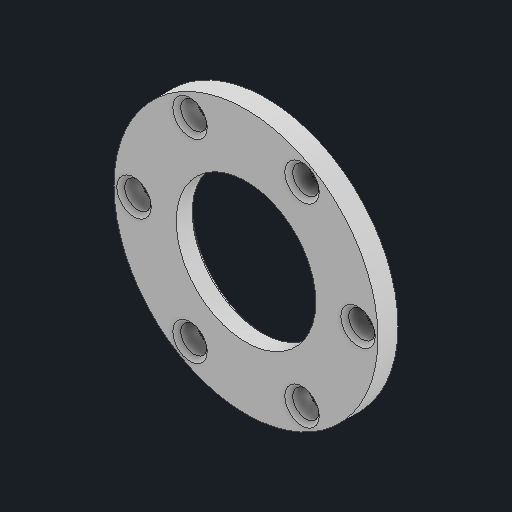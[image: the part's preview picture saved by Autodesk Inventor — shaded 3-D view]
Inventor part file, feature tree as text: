
AUTODESK INVENTOR PART (.ipt)
format: ipt  version: 2024.1 (Build 281209000, 209)  size: 168,960 bytes
history: native  units: in
note: dims shown in document units (in); Inventor stores cm internally (conversion verified against a paired STEP export)
features: other x3, extrude x1, chamfer x1, sketch x1, reference x1
ambient origin geometry x8: Origin, YZ Plane, XZ Plane, XY Plane, X Axis, Y Axis, Z Axis, Center Point
bodies: Solid1 (feature_tree)
feature tree (7):
  extrude  "Extrusion1"  Depth=0.125in
  chamfer  "Chamfer1"  Distance=0.1654in
  sketch  "Sketch1"  dims[d1=1.65in d2=0.1654in d3=0.1654in d4=0.1654in d5=0.1654in d6=0.1654in d7=0.1654in d8=0.125in d9=0.0in d10=0.025in d11=0.125in d12=45.0deg]
  reference  "Reference1"
  other  "<userpath>\Documents\School\FallCAD\Trebuchet\Trebuchet.iam"
  other  "Trebuchet.iam"
  other  "FrameTop:3"
